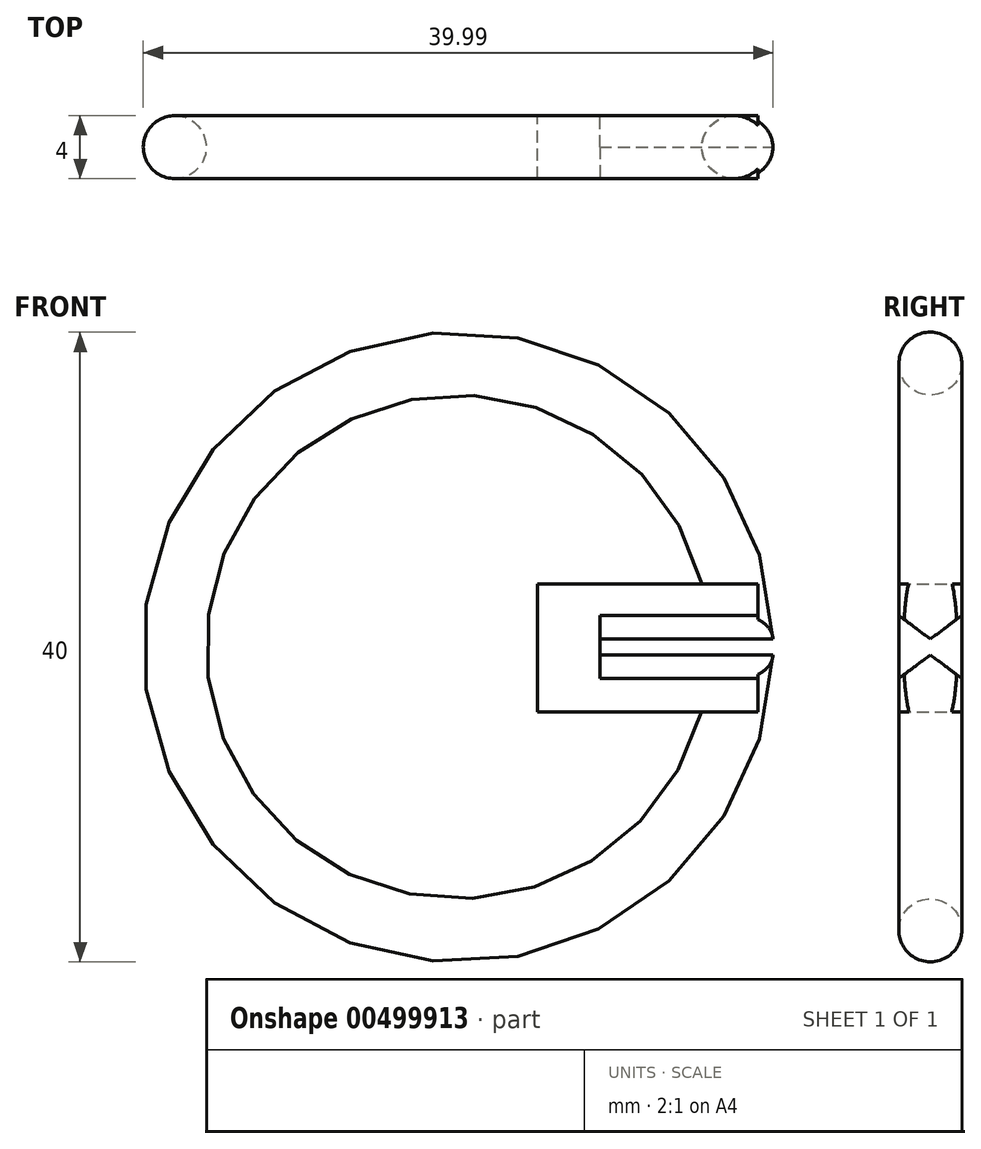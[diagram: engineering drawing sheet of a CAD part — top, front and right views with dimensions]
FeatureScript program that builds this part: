
annotation { "Feature Type Name" : "Feature", "Feature Type Description" : "" }
export const myFeature = defineFeature(function(context is Context, id is Id, definition is map)
    precondition{}
    {
        {
            var Q0;
            Q0=qCreatedBy(makeId("Top.planeOp"),FACE);
            var sketch = newSketch(context, id + "F0", { "sketchPlane" : qUnion([Q0])});
            skCircle(sketch, "E0", {"center": v(0, 0) * mm, "radius": 2 * mm});
            skLineSegment(sketch, "E1", {"start": v(2, 0) * mm, "end": v(2, 4.88) * mm});
            skLineSegment(sketch, "E2", {"start": v(-18, 0) * mm, "end": v(-18, 2.6) * mm});
            skSolve(sketch);
        }
        {
            var Q0;
            Q0 = qSketchRegion(id + "F0", true);
            var Q1;
            Q1=sQuery(id+"F0.wireOp",EDGE,"E2");
            revolve(context, id + "F1", {"entities" : qUnion([Q0]), "axis" : qUnion([Q1]), "revolveType" : RevolveType.FULL});
        }
        {
            var Q0;
            Q0=qCreatedBy(makeId("Front.planeOp"),FACE);
            var sketch = newSketch(context, id + "F2", { "sketchPlane" : qUnion([Q0])});
            skLineSegment(sketch, "E3.bottom", {"start": v(-12.97, 4) * mm, "end": v(1.03, 4) * mm});
            skLineSegment(sketch, "E3.top", {"start": v(-12.97, -4.11) * mm, "end": v(1.03, -4.11) * mm});
            skLineSegment(sketch, "E3.left", {"start": v(-12.97, -4) * mm, "end": v(-12.97, -4.11) * mm});
            skLineSegment(sketch, "E3.right", {"start": v(1.03, 4) * mm, "end": v(1.03, -4.11) * mm});
            skPoint(sketch, "E4.start.orphan", {"position": v(1.03, 0) * mm});
            skLineSegment(sketch, "E5", {"start": v(-12.97, 4) * mm, "end": v(-12.97, -4.11) * mm});
            skSolve(sketch);
        }
        {
            var Q0;
            Q0 = qSketchRegion(id + "F2", true);
            extrude(context, id + "F3", {"entities" : qUnion([Q0]), "operationType" : NewBodyOperationType.ADD, "depth" : 2 * mm, "hasSecondDirection" : true, "secondDirectionOppositeDirection" : true, "secondDirectionDepth" : 2 * mm});
        }
        {
            var Q0;
            Q0=qCreatedBy(makeId("Right.planeOp"),FACE);
            cPlane(context, id + "F4", {"entities" : qUnion([Q0]), "cplaneType" : CPlaneType.OFFSET, "offset" : 25 * mm, "width" : 150 * mm, "height" : 150 * mm});
        }
        {
            var Q0;
            Q0=qCreatedBy(id+"F4.planeOp",FACE);
            var sketch = newSketch(context, id + "F5", { "sketchPlane" : qUnion([Q0])});
            skPoint(sketch, "E6.endSnap0", {"position": v(-1, 0) * mm});
            skLineSegment(sketch, "E7.left", {"start": v(-2, 2) * mm, "end": v(-2, -2) * mm});
            skLineSegment(sketch, "E7.right", {"start": v(2, 2) * mm, "end": v(2, -2) * mm});
            skPoint(sketch, "E7.middle", {"position": v(0, 0) * mm});
            skLineSegment(sketch, "E8", {"start": v(0, 0.5) * mm, "end": v(-2, 2) * mm});
            skLineSegment(sketch, "E9", {"start": v(0, 0.5) * mm, "end": v(2, 2) * mm});
            skLineSegment(sketch, "E10", {"start": v(0, -0.5) * mm, "end": v(2, -2) * mm});
            skLineSegment(sketch, "E11", {"start": v(0, -0.5) * mm, "end": v(-2, -2) * mm});
            skPoint(sketch, "E6.end.orphan", {"position": v(2, 0) * mm});
            skPoint(sketch, "E12.end.orphan", {"position": v(-2, 0) * mm});
            skSolve(sketch);
        }
        {
            var Q0;
            Q0 = qSketchRegion(id + "F5", true);
            extrude(context, id + "F6", {"entities" : qUnion([Q0]), "operationType" : NewBodyOperationType.REMOVE, "oppositeDirection" : true, "depth" : 34 * mm});
        }
    });
